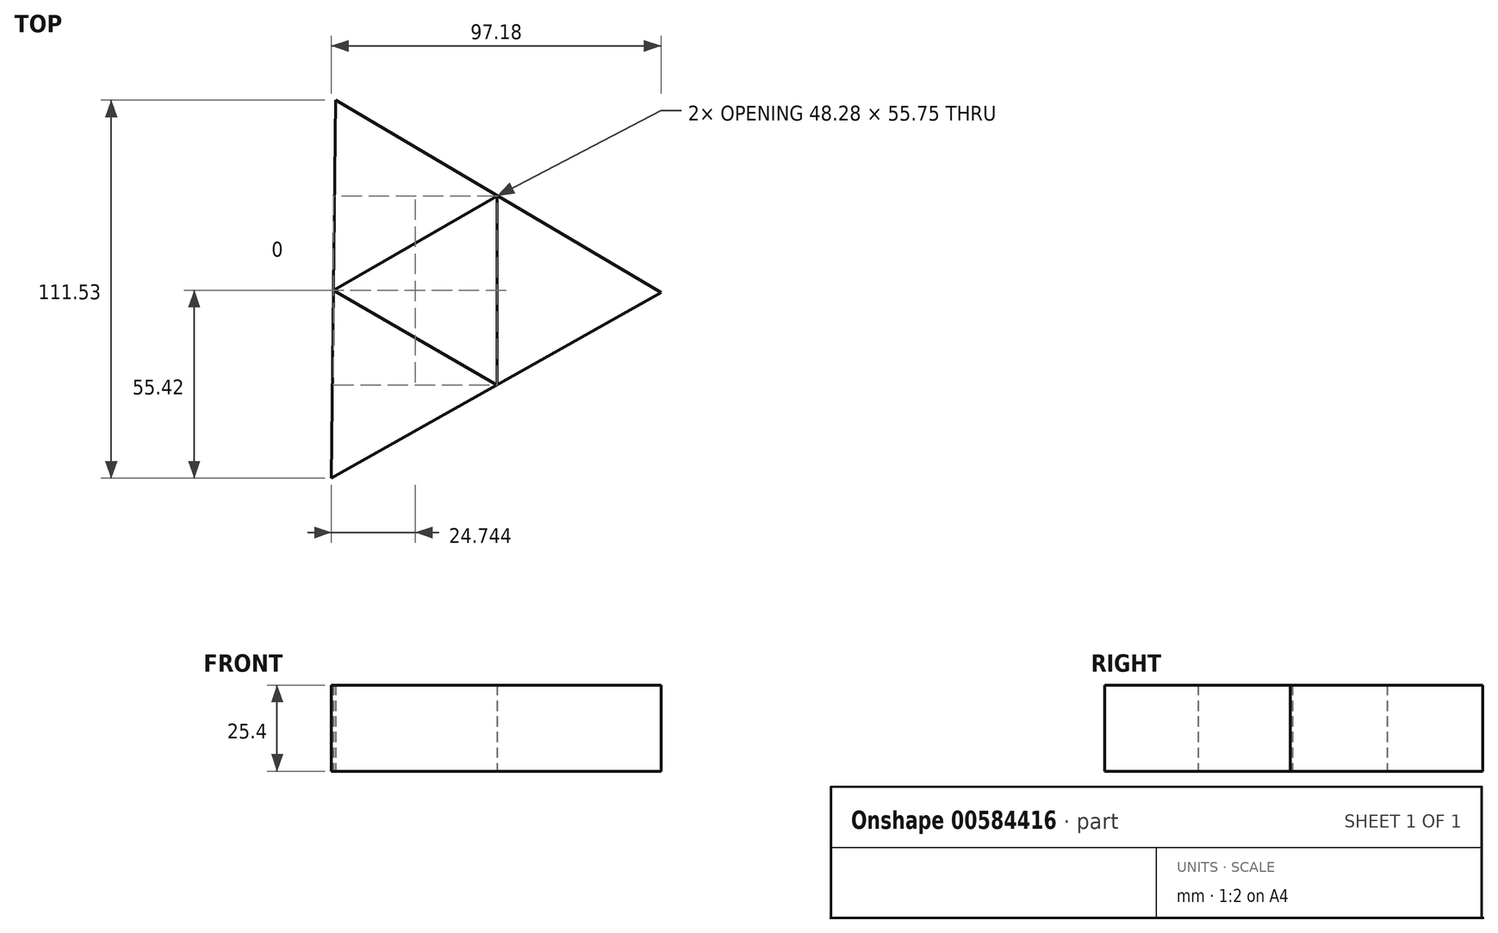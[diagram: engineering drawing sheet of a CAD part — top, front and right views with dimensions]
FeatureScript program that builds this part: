
annotation { "Feature Type Name" : "Feature", "Feature Type Description" : "" }
export const myFeature = defineFeature(function(context is Context, id is Id, definition is map)
    precondition{}
    {
        {
            var Q0;
            Q0=qCreatedBy(makeId("Top.planeOp"),FACE);
            var sketch = newSketch(context, id + "F0", { "sketchPlane" : qUnion([Q0])});
            skCircle(sketch, "E0.cCircle", {"center": v(0, 0) * mm, "radius": 32.2 * mm, "construction": true});
            skLineSegment(sketch, "E0.0", {"start": v(-31.6, 56.1) * mm, "end": v(64.4, -0.68) * mm});
            skLineSegment(sketch, "E0.1", {"start": v(64.4, -0.68) * mm, "end": v(-32.79, -55.42) * mm});
            skLineSegment(sketch, "E0.2", {"start": v(-32.79, -55.42) * mm, "end": v(-31.6, 56.1) * mm});
            skPoint(sketch, "E0.0.midPoint", {"position": v(16.4, 27.71) * mm});
            skCircle(sketch, "E1.cCircle", {"center": v(0, 0) * mm, "radius": 16.1 * mm, "construction": true});
            skLineSegment(sketch, "E1.0", {"start": v(16.1, 27.87) * mm, "end": v(16.1, -27.87) * mm});
            skLineSegment(sketch, "E1.1", {"start": v(16.1, -27.87) * mm, "end": v(-32.18, 0) * mm});
            skLineSegment(sketch, "E1.2", {"start": v(-32.18, 0) * mm, "end": v(16.1, 27.87) * mm});
            skPoint(sketch, "E1.0.midPoint", {"position": v(16.1, 0) * mm});
            skLineSegment(sketch, "E2", {"start": v(0, 37.41) * mm, "end": v(33.63, 57.3) * mm});
            skLineSegment(sketch, "E3", {"start": v(33.63, 57.3) * mm, "end": v(33.63, 17.52) * mm});
            skLineSegment(sketch, "E4", {"start": v(30.94, -19.53) * mm, "end": v(39.53, -52.85) * mm});
            skLineSegment(sketch, "E5", {"start": v(39.53, -52.85) * mm, "end": v(0, -36.95) * mm});
            skSolve(sketch);
        }
        {
            var Q0;
            Q0=makeQuery(id+"F0.imprint","IMPRINT",FACE,{"disambiguationData":[TD([[makeQuery(id+"F0.imprint","IMPRINT",EDGE,{"derivedFrom":sQuery(id+"F0.wireOp",EDGE,"E0.0")}),-1.0]])]});
            extrude(context, id + "F1", {"entities" : qUnion([Q0]), "depth" : 25.4 * mm, "offsetDistance" : 25.4 * mm});
        }
    });
